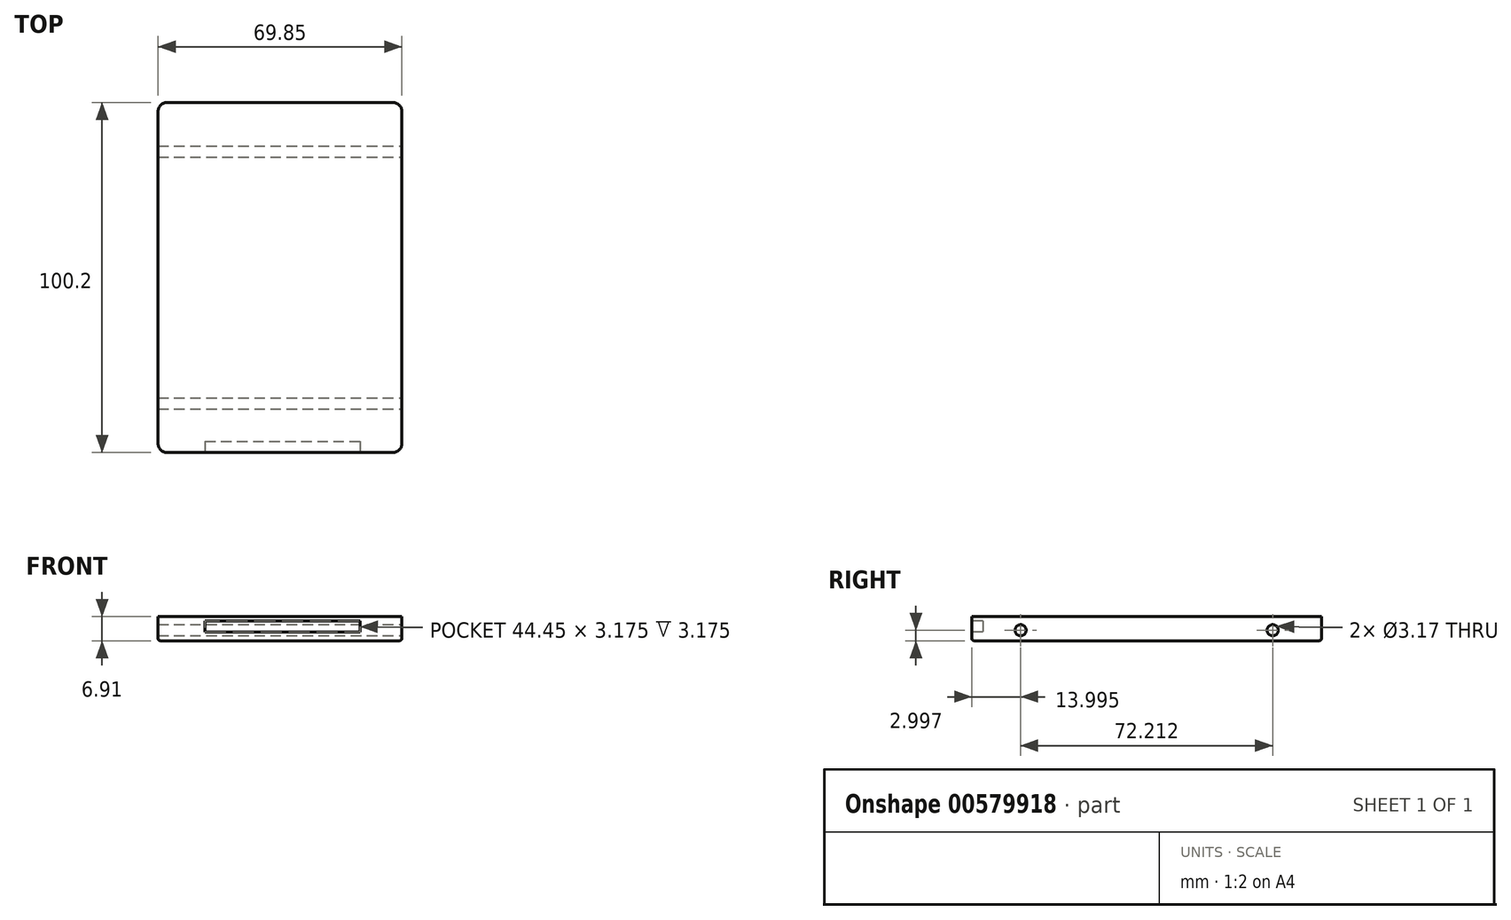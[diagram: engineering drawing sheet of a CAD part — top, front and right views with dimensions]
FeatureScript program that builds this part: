
annotation { "Feature Type Name" : "Feature", "Feature Type Description" : "" }
export const myFeature = defineFeature(function(context is Context, id is Id, definition is map)
    precondition{}
    {
        {
            var Q0;
            Q0=qCreatedBy(makeId("Top.planeOp"),FACE);
            var sketch = newSketch(context, id + "F0", { "sketchPlane" : qUnion([Q0])});
            skLineSegment(sketch, "E0.bottom", {"start": v(0, 0) * mm, "end": v(69.85, 0) * mm});
            skLineSegment(sketch, "E0.top", {"start": v(0, 100.2) * mm, "end": v(69.85, 100.2) * mm});
            skLineSegment(sketch, "E0.left", {"start": v(0, 0) * mm, "end": v(0, 100.2) * mm});
            skLineSegment(sketch, "E0.right", {"start": v(69.85, 0) * mm, "end": v(69.85, 100.2) * mm});
            skSolve(sketch);
        }
        {
            var Q0;
            Q0 = qSketchRegion(id + "F0", true);
            extrude(context, id + "F1", {"entities" : qUnion([Q0]), "depth" : 6.9 * mm, "offsetDistance" : 25.4 * mm});
        }
        {
            var Q0;
            Q0=makeQuery(id+"F1.opExtrude","SWEPT_EDGE",EDGE,{"disambiguationData":[OSD([sQuery(id+"F0.wireOp",EDGE,"E0.bottom"),sQuery(id+"F0.wireOp",EDGE,"E0.right")])]});
            var Q1;
            Q1=makeQuery(id+"F1.opExtrude","SWEPT_EDGE",EDGE,{"disambiguationData":[OSD([sQuery(id+"F0.wireOp",EDGE,"E0.bottom"),sQuery(id+"F0.wireOp",EDGE,"E0.left")])]});
            var Q2;
            Q2=makeQuery(id+"F1.opExtrude","SWEPT_EDGE",EDGE,{"disambiguationData":[OSD([sQuery(id+"F0.wireOp",EDGE,"E0.top"),sQuery(id+"F0.wireOp",EDGE,"E0.right")])]});
            var Q3;
            Q3=makeQuery(id+"F1.opExtrude","SWEPT_EDGE",EDGE,{"disambiguationData":[OSD([sQuery(id+"F0.wireOp",EDGE,"E0.top"),sQuery(id+"F0.wireOp",EDGE,"E0.left")])]});
            fillet(context, id + "F2", {"entities" : qUnion([Q0, Q1, Q2, Q3]), "radius" : 2.54 * mm, "tangentPropagation" : true, "allowEdgeOverflow" : false});
        }
        {
            var Q0;
            Q0=makeQuery(id+"F1.opExtrude","SWEPT_FACE",FACE,{"disambiguationData":[OSD([sQuery(id+"F0.wireOp",EDGE,"E0.right")])]});
            var sketch = newSketch(context, id + "F3", { "sketchPlane" : qUnion([Q0])});
            skCircle(sketch, "E1", {"center": v(14, 3) * mm, "radius": 1.59 * mm});
            skCircle(sketch, "E2", {"center": v(86.2, 3) * mm, "radius": 1.59 * mm});
            skSolve(sketch);
        }
        {
            var Q0;
            Q0 = qSketchRegion(id + "F3", true);
            extrude(context, id + "F4", {"entities" : qUnion([Q0]), "operationType" : NewBodyOperationType.REMOVE, "endBound" : BoundingType.THROUGH_ALL, "oppositeDirection" : true, "depth" : 25.4 * mm, "offsetDistance" : 25.4 * mm});
        }
        {
            var Q0;
            Q0=makeQuery(id+"F1.opExtrude","CAP_EDGE",EDGE,{"disambiguationData":[OSD([sQuery(id+"F0.wireOp",EDGE,"E0.right")])],"isStart":true});
            var Q1;
            {var subQ0=sQuery(id+"F0.wireOp",EDGE,"E0.right");var subQ1=sQuery(id+"F0.wireOp",EDGE,"E0.bottom");Q1=makeQuery(id+"F2.opFillet","BLEND_EDGE",EDGE,{"blendedFrom":[makeQuery(id+"F1.opExtrude","SWEPT_EDGE",EDGE,{"disambiguationData":[OSD([subQ1,subQ0])]}),makeQuery(id+"F1.opExtrude","CAP_FACE",FACE,{"disambiguationData":[OSD([subQ1,sQuery(id+"F0.wireOp",EDGE,"E0.top"),sQuery(id+"F0.wireOp",EDGE,"E0.left"),subQ0])],"isStart":true})],"blendedInto":[makeQuery(id+"F1.opExtrude","CAP_FACE",FACE,{"disambiguationData":[OSD([subQ1,sQuery(id+"F0.wireOp",EDGE,"E0.top"),sQuery(id+"F0.wireOp",EDGE,"E0.left"),subQ0])],"isStart":true})]});}
            var Q2;
            Q2=makeQuery(id+"F1.opExtrude","CAP_EDGE",EDGE,{"disambiguationData":[OSD([sQuery(id+"F0.wireOp",EDGE,"E0.bottom")])],"isStart":true});
            var Q3;
            {var subQ0=sQuery(id+"F0.wireOp",EDGE,"E0.left");var subQ1=sQuery(id+"F0.wireOp",EDGE,"E0.bottom");Q3=makeQuery(id+"F2.opFillet","BLEND_EDGE",EDGE,{"blendedFrom":[makeQuery(id+"F1.opExtrude","SWEPT_EDGE",EDGE,{"disambiguationData":[OSD([subQ1,subQ0])]}),makeQuery(id+"F1.opExtrude","CAP_FACE",FACE,{"disambiguationData":[OSD([subQ1,sQuery(id+"F0.wireOp",EDGE,"E0.top"),subQ0,sQuery(id+"F0.wireOp",EDGE,"E0.right")])],"isStart":true})],"blendedInto":[makeQuery(id+"F1.opExtrude","CAP_FACE",FACE,{"disambiguationData":[OSD([subQ1,sQuery(id+"F0.wireOp",EDGE,"E0.top"),subQ0,sQuery(id+"F0.wireOp",EDGE,"E0.right")])],"isStart":true})]});}
            var Q4;
            Q4=makeQuery(id+"F1.opExtrude","CAP_EDGE",EDGE,{"disambiguationData":[OSD([sQuery(id+"F0.wireOp",EDGE,"E0.left")])],"isStart":true});
            var Q5;
            {var subQ0=sQuery(id+"F0.wireOp",EDGE,"E0.left");var subQ1=sQuery(id+"F0.wireOp",EDGE,"E0.top");Q5=makeQuery(id+"F2.opFillet","BLEND_EDGE",EDGE,{"blendedFrom":[makeQuery(id+"F1.opExtrude","SWEPT_EDGE",EDGE,{"disambiguationData":[OSD([subQ1,subQ0])]}),makeQuery(id+"F1.opExtrude","CAP_FACE",FACE,{"disambiguationData":[OSD([sQuery(id+"F0.wireOp",EDGE,"E0.bottom"),subQ1,subQ0,sQuery(id+"F0.wireOp",EDGE,"E0.right")])],"isStart":true})],"blendedInto":[makeQuery(id+"F1.opExtrude","CAP_FACE",FACE,{"disambiguationData":[OSD([sQuery(id+"F0.wireOp",EDGE,"E0.bottom"),subQ1,subQ0,sQuery(id+"F0.wireOp",EDGE,"E0.right")])],"isStart":true})]});}
            var Q6;
            Q6=makeQuery(id+"F1.opExtrude","CAP_EDGE",EDGE,{"disambiguationData":[OSD([sQuery(id+"F0.wireOp",EDGE,"E0.top")])],"isStart":true});
            var Q7;
            {var subQ0=sQuery(id+"F0.wireOp",EDGE,"E0.right");var subQ1=sQuery(id+"F0.wireOp",EDGE,"E0.top");Q7=makeQuery(id+"F2.opFillet","BLEND_EDGE",EDGE,{"blendedFrom":[makeQuery(id+"F1.opExtrude","SWEPT_EDGE",EDGE,{"disambiguationData":[OSD([subQ1,subQ0])]}),makeQuery(id+"F1.opExtrude","CAP_FACE",FACE,{"disambiguationData":[OSD([sQuery(id+"F0.wireOp",EDGE,"E0.bottom"),subQ1,sQuery(id+"F0.wireOp",EDGE,"E0.left"),subQ0])],"isStart":true})],"blendedInto":[makeQuery(id+"F1.opExtrude","CAP_FACE",FACE,{"disambiguationData":[OSD([sQuery(id+"F0.wireOp",EDGE,"E0.bottom"),subQ1,sQuery(id+"F0.wireOp",EDGE,"E0.left"),subQ0])],"isStart":true})]});}
            fillet(context, id + "F5", {"entities" : qUnion([Q0, Q1, Q2, Q3, Q4, Q5, Q6, Q7]), "radius" : 0.64 * mm, "tangentPropagation" : true, "allowEdgeOverflow" : false});
        }
        {
            var Q0;
            Q0=makeQuery(id+"F1.opExtrude","SWEPT_FACE",FACE,{"disambiguationData":[OSD([sQuery(id+"F0.wireOp",EDGE,"E0.bottom")])]});
            var sketch = newSketch(context, id + "F6", { "sketchPlane" : qUnion([Q0])});
            skLineSegment(sketch, "E3.bottom", {"start": v(13.44, 5.64) * mm, "end": v(57.89, 5.64) * mm});
            skLineSegment(sketch, "E3.top", {"start": v(13.44, 2.46) * mm, "end": v(57.89, 2.46) * mm});
            skLineSegment(sketch, "E3.left", {"start": v(13.44, 5.64) * mm, "end": v(13.44, 2.46) * mm});
            skLineSegment(sketch, "E3.right", {"start": v(57.89, 5.64) * mm, "end": v(57.89, 2.46) * mm});
            skSolve(sketch);
        }
        {
            var Q0;
            Q0 = qSketchRegion(id + "F6", true);
            extrude(context, id + "F7", {"entities" : qUnion([Q0]), "operationType" : NewBodyOperationType.REMOVE, "oppositeDirection" : true, "depth" : 3.17 * mm, "offsetDistance" : 25.4 * mm});
        }
    });
